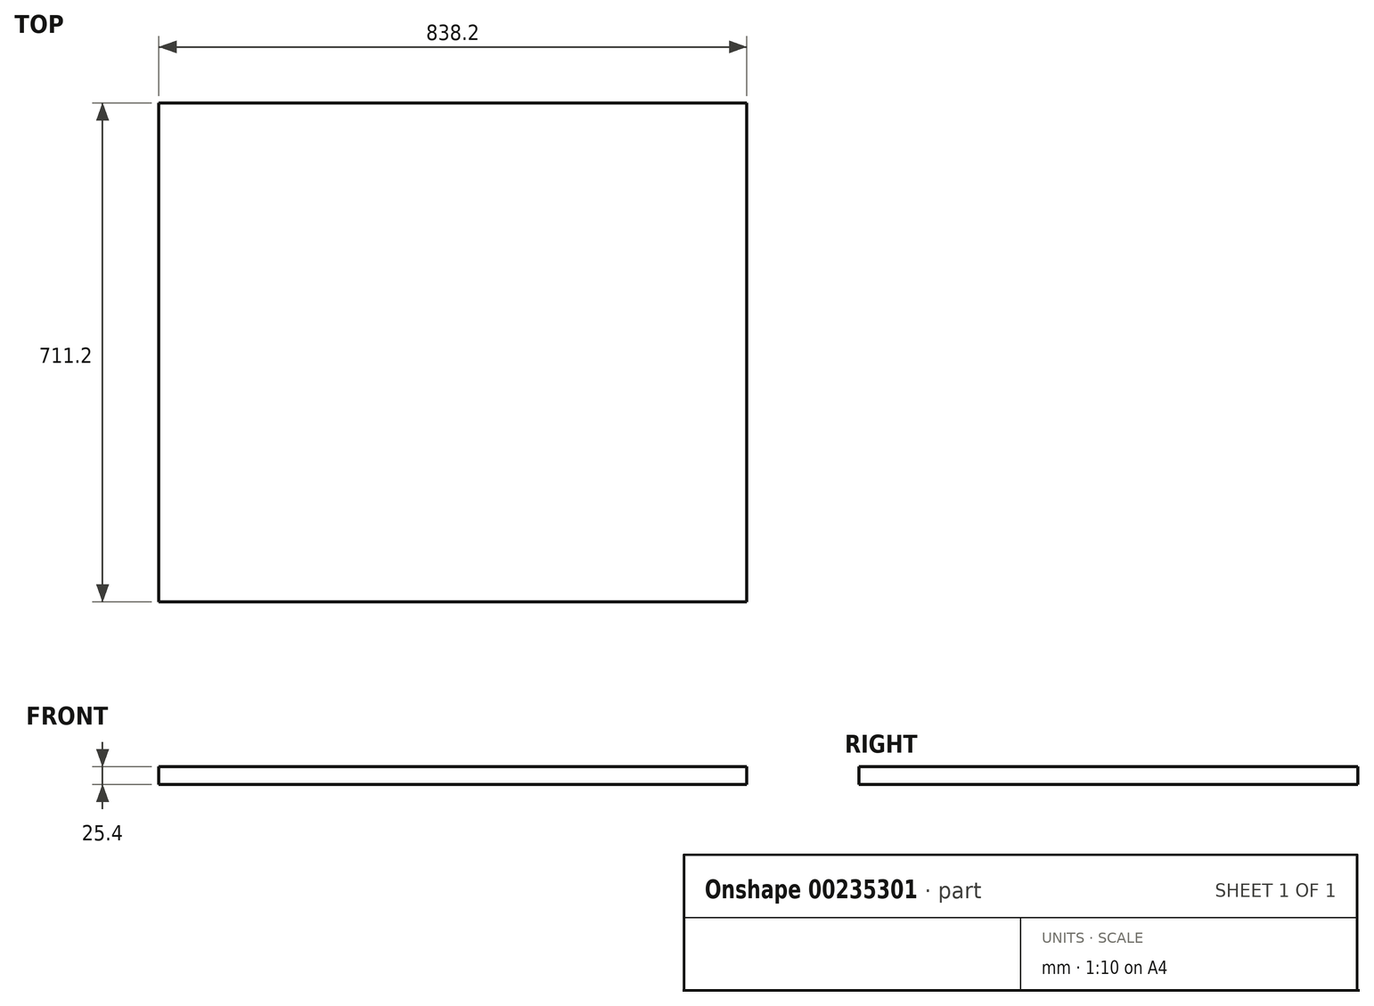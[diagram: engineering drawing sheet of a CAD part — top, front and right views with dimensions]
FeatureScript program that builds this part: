
annotation { "Feature Type Name" : "Feature", "Feature Type Description" : "" }
export const myFeature = defineFeature(function(context is Context, id is Id, definition is map)
    precondition{}
    {
        {
            var Q0;
            Q0=qCreatedBy(makeId("Top.planeOp"),FACE);
            var sketch = newSketch(context, id + "F0", { "sketchPlane" : qUnion([Q0])});
            skLineSegment(sketch, "E0.bottom", {"start": v(-411.2, 331.14) * mm, "end": v(427, 331.14) * mm});
            skLineSegment(sketch, "E0.top", {"start": v(-411.2, -380.06) * mm, "end": v(427, -380.06) * mm});
            skLineSegment(sketch, "E0.left", {"start": v(-411.2, 331.14) * mm, "end": v(-411.2, -380.06) * mm});
            skLineSegment(sketch, "E0.right", {"start": v(427, 331.14) * mm, "end": v(427, -380.06) * mm});
            skSolve(sketch);
        }
        {
            var Q0;
            Q0 = qSketchRegion(id + "F0", true);
            extrude(context, id + "F1", {"entities" : qUnion([Q0]), "depth" : 25.4 * mm});
        }
    });
